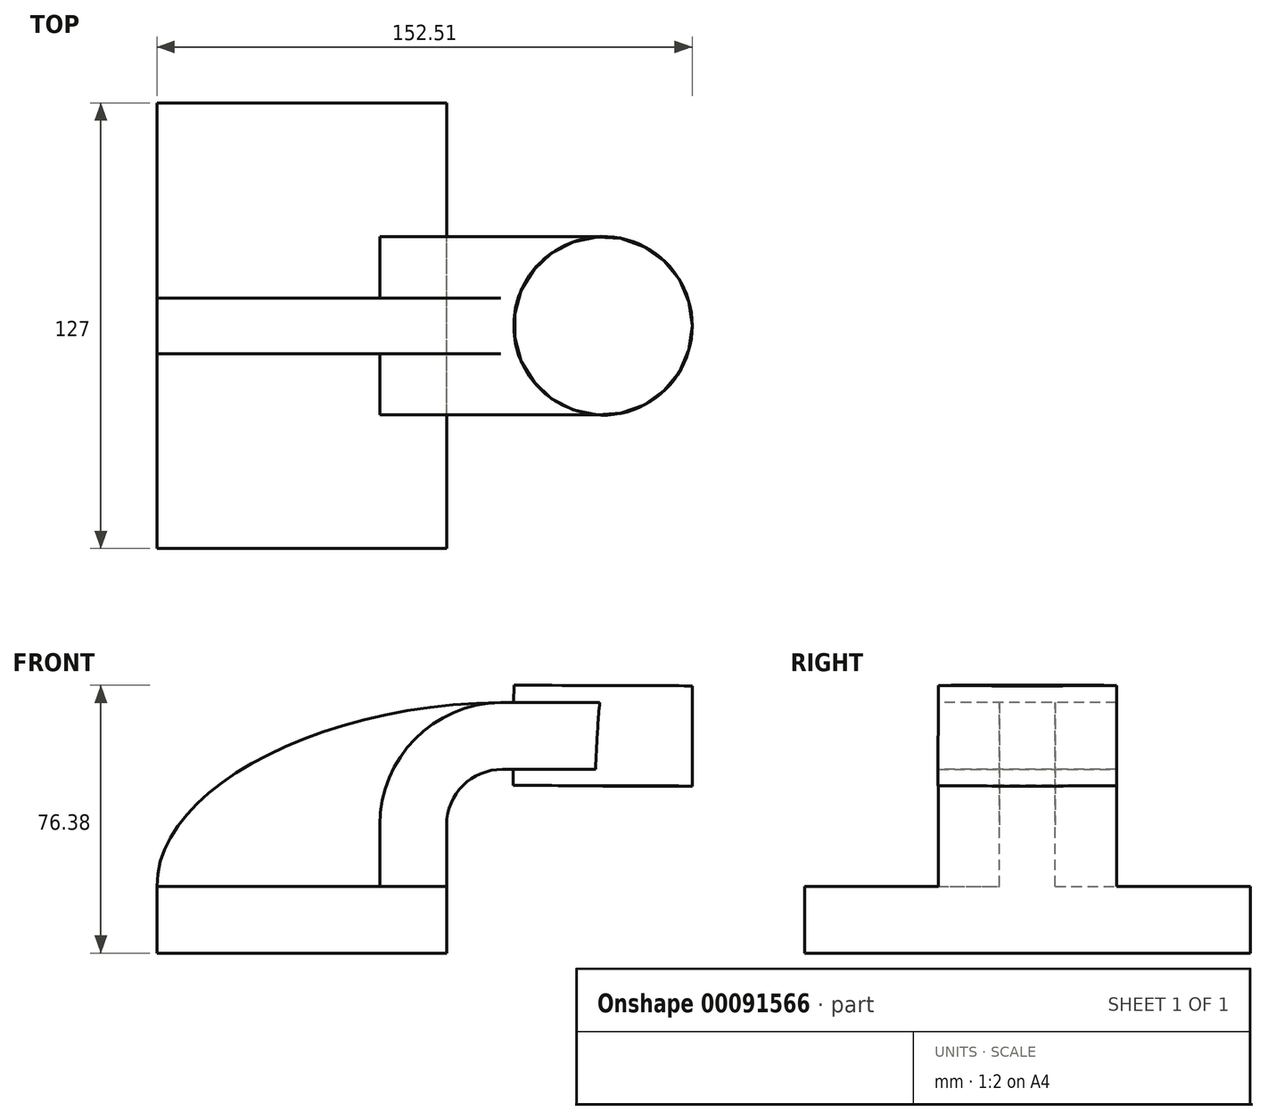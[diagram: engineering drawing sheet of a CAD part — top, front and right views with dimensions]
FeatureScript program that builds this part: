
annotation { "Feature Type Name" : "Feature", "Feature Type Description" : "" }
export const myFeature = defineFeature(function(context is Context, id is Id, definition is map)
    precondition{}
    {
        {
            var Q0;
            Q0=qCreatedBy(makeId("Front.planeOp"),FACE);
            var sketch = newSketch(context, id + "F0", { "sketchPlane" : qUnion([Q0])});
            skLineSegment(sketch, "E0.bottom", {"start": v(41.28, -9.52) * mm, "end": v(-41.27, -9.53) * mm});
            skLineSegment(sketch, "E0.top", {"start": v(41.27, 9.53) * mm, "end": v(-41.28, 9.53) * mm});
            skLineSegment(sketch, "E0.left", {"start": v(41.28, -9.52) * mm, "end": v(41.28, 9.53) * mm});
            skLineSegment(sketch, "E0.right", {"start": v(-41.27, -9.52) * mm, "end": v(-41.28, 9.53) * mm});
            skPoint(sketch, "E0.middle", {"position": v(0, 0) * mm});
            skLineSegment(sketch, "E1", {"start": v(41.27, 9.53) * mm, "end": v(41.27, 27) * mm});
            skArc(sketch, "E2", {"start": v(41.27, 27) * mm, "mid": v(45.92, 38.23) * mm, "end": v(57.15, 42.88) * mm});
            skArc(sketch, "E3.1", {"start": v(22.23, 27) * mm, "mid": v(32.45, 51.7) * mm, "end": v(57.15, 61.93) * mm});
            skLineSegment(sketch, "E3.2", {"start": v(22.22, 9.53) * mm, "end": v(22.22, 27) * mm});
            skLineSegment(sketch, "E4.bottom", {"start": v(60.43, 38.1) * mm, "end": v(111.23, 38.1) * mm});
            skLineSegment(sketch, "E4.top", {"start": v(60.43, 66.68) * mm, "end": v(111.23, 66.68) * mm});
            skLineSegment(sketch, "E4.left", {"start": v(60.43, 38.1) * mm, "end": v(60.43, 66.68) * mm});
            skLineSegment(sketch, "E4.right", {"start": v(111.23, 38.1) * mm, "end": v(111.23, 66.68) * mm});
            skPoint(sketch, "E4.middle", {"position": v(85.83, 52.39) * mm});
            skLineSegment(sketch, "E5", {"start": v(85.83, 66.68) * mm, "end": v(85.72, 38.1) * mm});
            skFitSpline(sketch, "E6", {"points": [v(-41.28, 9.53) * mm, v(57.15, 61.93) * mm], "startDerivative": vector(-0.58, 81.83) * mm, "endDerivative": vector(157.8, 0.95) * mm});
            skLineSegment(sketch, "E7", {"start": v(57.15, 61.93) * mm, "end": v(85.72, 61.93) * mm});
            skLineSegment(sketch, "E8", {"start": v(85.72, 61.93) * mm, "end": v(85.72, 42.88) * mm});
            skLineSegment(sketch, "E9", {"start": v(57.15, 42.88) * mm, "end": v(85.72, 42.88) * mm});
            skSolve(sketch);
        }
        {
            var Q0;
            Q0=makeQuery(id+"F0.imprint","IMPRINT",FACE,{"disambiguationData":[TD([[makeQuery(id+"F0.imprint","IMPRINT",EDGE,{"derivedFrom":sQuery(id+"F0.wireOp",EDGE,"E0.bottom")}),-1.0]])]});
            extrude(context, id + "F1", {"entities" : qUnion([Q0]), "endBound" : BoundingType.SYMMETRIC, "depth" : 127 * mm});
        }
        {
            var Q0;
            {var subQ10=sQuery(id+"F0.wireOp",EDGE,"E1");Q0=makeQuery(id+"F0.imprint","IMPRINT",FACE,{"disambiguationData":[TD([[makeQuery(id+"F0.imprint","IMPRINT",EDGE,{"derivedFrom":subQ10}),1.0]])]});}
            var Q1;
            {var subQ5=sQuery(id+"F0.wireOp",EDGE,"E8");Q1=makeQuery(id+"F0.imprint","IMPRINT",FACE,{"disambiguationData":[TD([[makeQuery(id+"F0.imprint","IMPRINT",EDGE,{"derivedFrom":subQ5}),-1.0]])]});}
            extrude(context, id + "F2", {"entities" : qUnion([Q0, Q1]), "operationType" : NewBodyOperationType.ADD, "endBound" : BoundingType.SYMMETRIC, "depth" : 50.8 * mm});
        }
        {
            var Q0;
            {var subQ3=sQuery(id+"F0.wireOp",EDGE,"E3.2");Q0=makeQuery(id+"F0.imprint","IMPRINT",FACE,{"disambiguationData":[TD([[makeQuery(id+"F0.imprint","IMPRINT",EDGE,{"derivedFrom":subQ3}),1.0]])]});}
            extrude(context, id + "F3", {"entities" : qUnion([Q0]), "operationType" : NewBodyOperationType.ADD, "endBound" : BoundingType.SYMMETRIC, "depth" : 15.88 * mm});
        }
        {
            var Q0;
            {var subQ0=sQuery(id+"F0.wireOp",EDGE,"E4.right");Q0=makeQuery(id+"F0.imprint","IMPRINT",FACE,{"disambiguationData":[TD([[makeQuery(id+"F0.imprint","IMPRINT",EDGE,{"derivedFrom":subQ0}),1.0]])]});}
            var Q1;
            Q1=sQuery(id+"F0.wireOp",EDGE,"E5");
            revolve(context, id + "F4", {"operationType" : NewBodyOperationType.ADD, "entities" : qUnion([Q0]), "axis" : qUnion([Q1]), "revolveType" : RevolveType.FULL});
        }
    });
